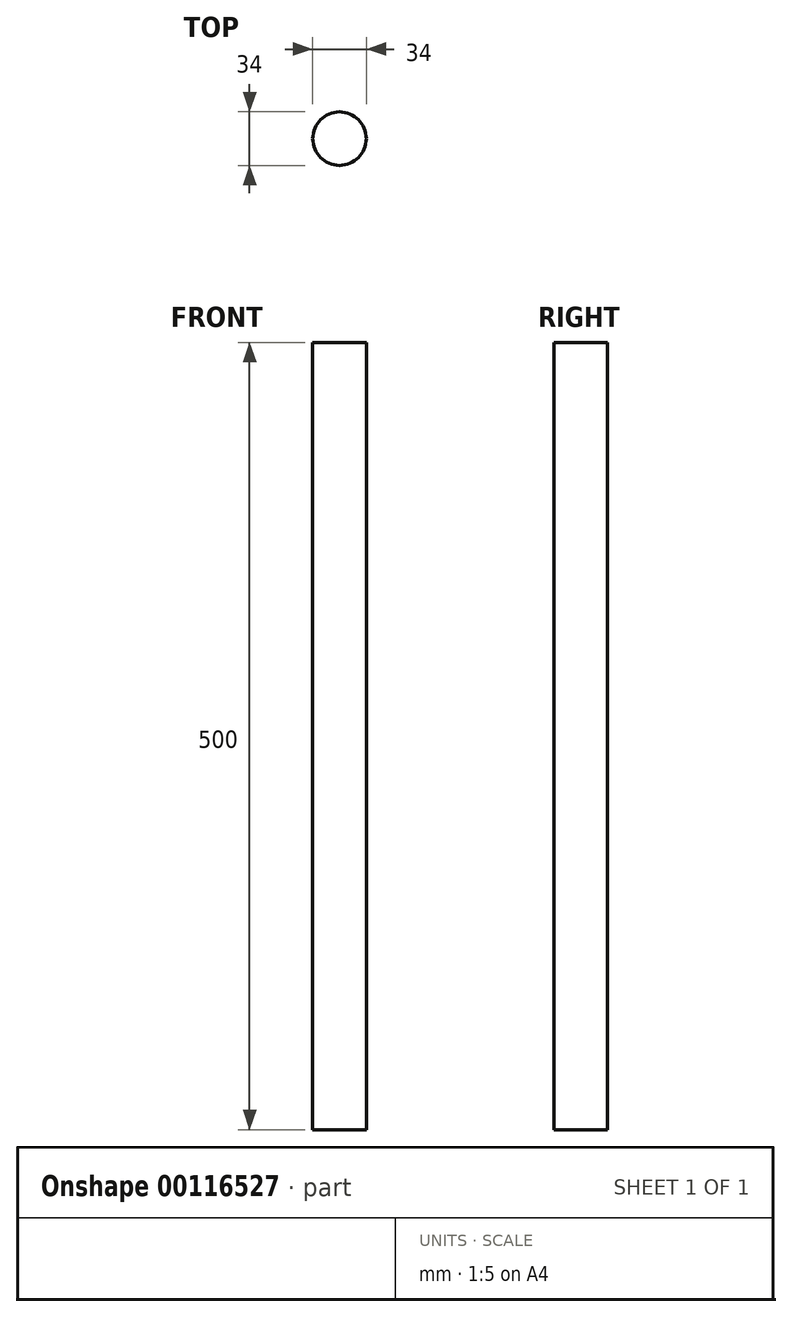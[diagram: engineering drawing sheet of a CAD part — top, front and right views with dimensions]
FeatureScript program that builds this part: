
annotation { "Feature Type Name" : "Feature", "Feature Type Description" : "" }
export const myFeature = defineFeature(function(context is Context, id is Id, definition is map)
    precondition{}
    {
        {
            var Q0;
            Q0=qCreatedBy(makeId("Top.planeOp"),FACE);
            var sketch = newSketch(context, id + "F0", { "sketchPlane" : qUnion([Q0])});
            skCircle(sketch, "E0", {"center": v(0, 0) * mm, "radius": 17 * mm});
            skSolve(sketch);
        }
        {
            var Q0;
            Q0=makeQuery(id+"F0.imprint","IMPRINT",FACE,{"disambiguationData":[TD([[makeQuery(id+"F0.imprint","IMPRINT",EDGE,{"derivedFrom":sQuery(id+"F0.wireOp",EDGE,"E0")}),1.0]])]});
            var Q1;
            Q1=sQuery(id+"F0.wireOp",EDGE,"E0");
            extrude(context, id + "F1", {"entities" : qUnion([Q0]), "surfaceEntities" : qUnion([Q1]), "depth" : 500 * mm});
        }
    });
